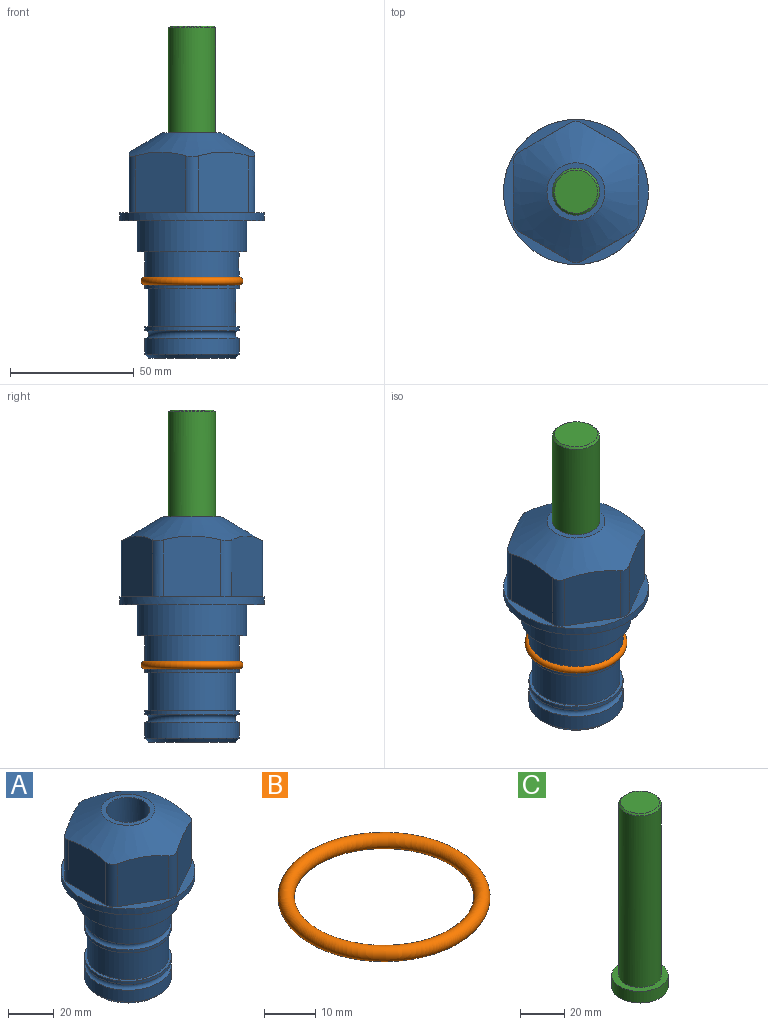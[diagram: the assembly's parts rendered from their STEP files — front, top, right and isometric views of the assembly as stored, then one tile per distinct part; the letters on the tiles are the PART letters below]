
ASSEMBLY  parts=3 mates=1
PART A: 36 faces, bbox 58.7x58.7x91.2 mm
  f0: cylinder r=17.78mm len=35.56mm, axis (0,0,1), area 1670.8mm2, adj f23,f24,f31
  f1: cylinder r=19.05mm len=38.1mm, axis (0,0,1), area 1191.9mm2, adj f26,f27,f30
  f2: plane 58.66x58.66mm, normal (0,0,-1), area 1150.6mm2, adj f3,f28
  f3: cylinder r=29.33mm len=58.66mm, axis (0,0,-1), area 585.1mm2, adj f2,f4
  f4: plane 58.66x58.66mm, normal (0,0,1), area 475.9mm2, adj f3,f5,f6,f7,f8,f9,f10,f11
  f5: plane 24.5x20.32mm, normal (-0.5,0.87,0), area 562.8mm2, adj f4,f15,f16,f17
  f6: plane 24.5x20.32mm, normal (0.5,0.87,0), area 562.8mm2, adj f4,f14,f15,f17
  f7: plane 24.5x23.48mm, normal (1,0,0), area 562.8mm2, adj f4,f13,f14,f17
  f8: plane 24.5x20.32mm, normal (0.5,-0.87,0), area 562.8mm2, adj f4,f12,f13,f17
  f9: plane 24.5x20.32mm, normal (-0.5,-0.87,0), area 562.8mm2, adj f4,f11,f12,f17
  f10: plane 24.5x23.48mm, normal (-1,0,0), area 562.8mm2, adj f4,f11,f16,f17
  f11: cylinder r=5.08mm len=23.01mm, axis (0,0,-1), area 121.2mm2, adj f4,f9,f10,f17
  f12: cylinder r=5.08mm len=23.01mm, axis (0,0,-1), area 121.2mm2, adj f4,f8,f9,f17
  f13: cylinder r=5.08mm len=23.01mm, axis (0,0,-1), area 121.2mm2, adj f4,f7,f8,f17
  f14: cylinder r=5.08mm len=23.01mm, axis (0,0,-1), area 121.2mm2, adj f4,f6,f7,f17
  f15: cylinder r=5.08mm len=23.01mm, axis (0,0,-1), area 121.2mm2, adj f4,f5,f6,f17
  f16: cylinder r=5.08mm len=23.01mm, axis (0,0,-1), area 121.2mm2, adj f4,f5,f10,f17
  f17: cone r=11.73mm half-angle=60deg, axis (0,0,-1), area 2071.8mm2, adj f5,f6,f7,f8,f9,f10,f11,f12
  f18: plane 23.46x23.46mm, normal (0,0,1), area 147.4mm2, adj f17,f35
  f19: plane 34.93x34.93mm, normal (0,0,-1), area 958mm2, adj f29
  f20: cylinder r=19.05mm len=38.1mm, axis (0,0,1), area 760.1mm2, adj f21,f29
  f21: torus R=19.05mm, axis (0,0,1), area 565.3mm2, adj f20,f22
  f22: cylinder r=19.05mm len=38.1mm, axis (0,0,1), area 190mm2, adj f21,f23
  f23: plane 38.1x38.1mm, normal (0,0,1), area 146.9mm2, adj f0,f22
  f24: plane 38.1x38.1mm, normal (0,0,-1), area 146.9mm2, adj f0,f25
  f25: cylinder r=19.05mm len=38.1mm, axis (0,0,1), area 190mm2, adj f24,f26
  f26: torus R=19.05mm, axis (0,0,1), area 565.3mm2, adj f1,f25
  f27: plane 44.45x44.45mm, normal (0,0,-1), area 411.7mm2, adj f1,f28
  f28: cylinder r=22.23mm len=44.45mm, axis (0,0,1), area 1773.5mm2, adj f2,f27
  f29: cone r=19.05mm half-angle=45deg, axis (0,0,1), area 257.5mm2, adj f19,f20
  f30: cylinder r=3.17mm len=6.75mm, axis (-1,0,0), area 128mm2, adj f1,f33
  f31: cylinder r=3.17mm len=6.35mm, axis (-1,0,0), area 102.5mm2, adj f0,f33
  f32: plane 25.4x25.4mm, normal (0,0,1), area 506.7mm2, adj f33
  f33: cylinder r=12.7mm len=66.42mm, axis (0,0,-1), area 5236.2mm2, adj f30,f31,f32,f34
  f34: cone r=9.53mm half-angle=30deg, axis (0,0,-1), area 443.4mm2, adj f33,f35
  f35: cylinder r=9.53mm len=19.05mm, axis (0,0,-1), area 849mm2, adj f18,f34
PART B: 1 faces, bbox 44.7x44.7x3.2 mm
  f0: torus R=19.05mm, axis (0,0,1), area 1193.9mm2
PART C: 6 faces, bbox 25.4x25.4x101.6 mm
  f0: plane 17.46x17.46mm, normal (0,0,1), area 239.5mm2, adj f5
  f1: plane 25.4x25.4mm, normal (0,0,-1), area 506.7mm2, adj f2
  f2: cylinder r=12.7mm len=25.4mm, axis (0,0,1), area 506.7mm2, adj f1,f3
  f3: plane 25.4x25.4mm, normal (0,0,1), area 221.7mm2, adj f2,f4
  f4: cylinder r=9.53mm len=94.46mm, axis (0,0,1), area 5653mm2, adj f3,f5
  f5: cone r=8.73mm half-angle=45deg, axis (0,0,-1), area 64.4mm2, adj f0,f4
PLACE A at identity fixed
PLACE B at identity
PLACE C t=(0,0,5.03)mm
MATE cylindrical C.f2 <-> A.f0  axis (0,0,1) through (0,0,30.67)mm
